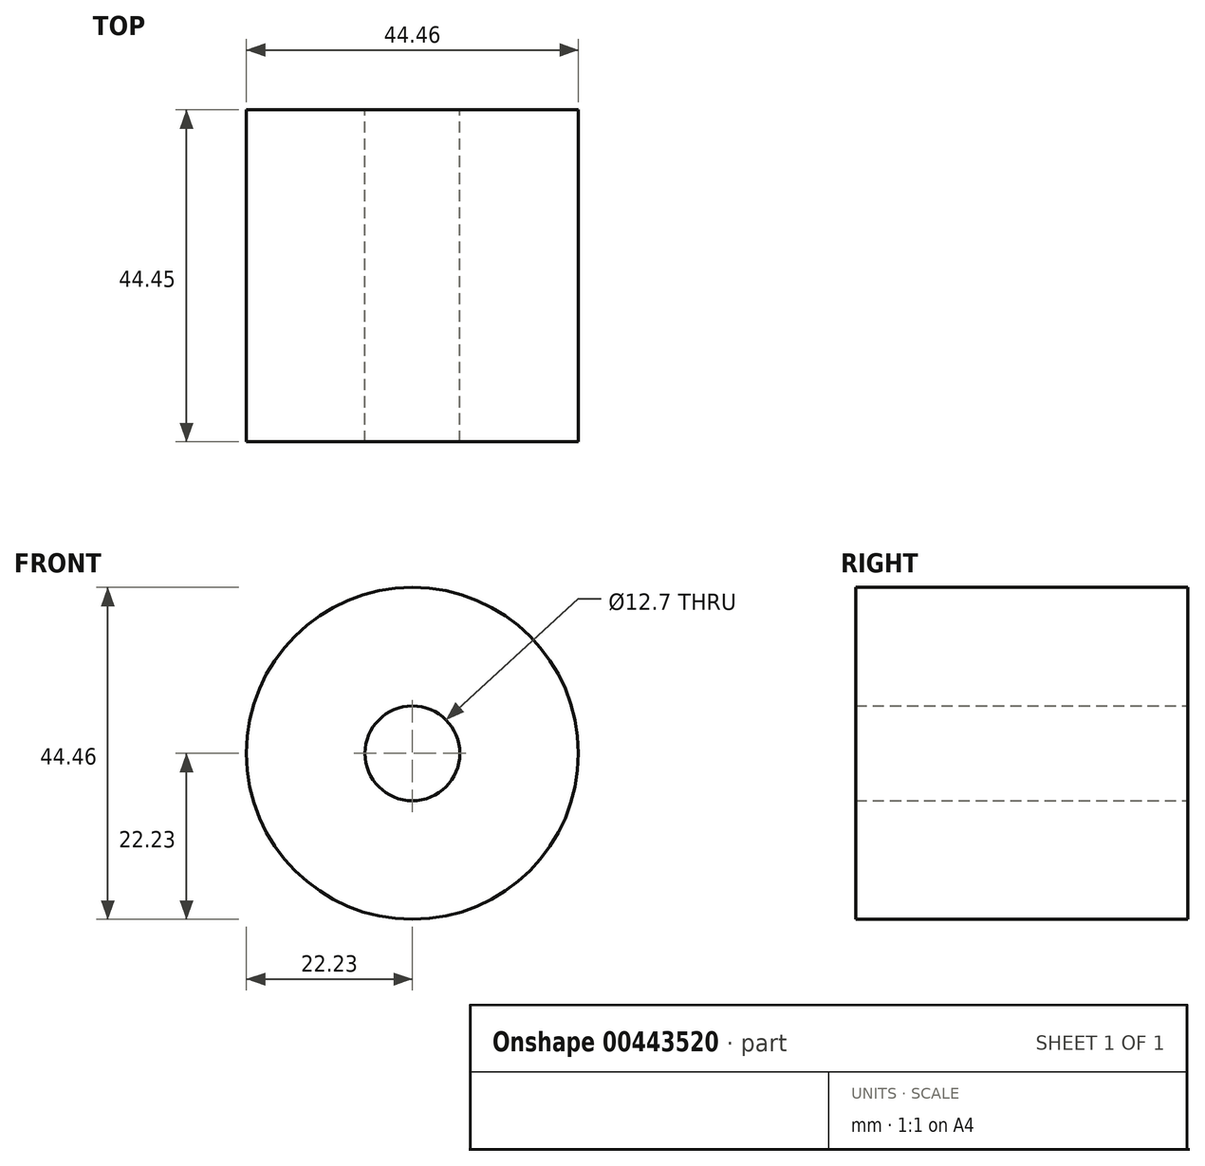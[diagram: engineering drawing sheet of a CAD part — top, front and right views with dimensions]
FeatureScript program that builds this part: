
annotation { "Feature Type Name" : "Feature", "Feature Type Description" : "" }
export const myFeature = defineFeature(function(context is Context, id is Id, definition is map)
    precondition{}
    {
        {
            var Q0;
            Q0=qCreatedBy(makeId("Front.planeOp"),FACE);
            var sketch = newSketch(context, id + "F0", { "sketchPlane" : qUnion([Q0])});
            skCircle(sketch, "E0", {"center": v(0, 0) * mm, "radius": 22.23 * mm});
            skCircle(sketch, "E1", {"center": v(0, 0) * mm, "radius": 6.35 * mm});
            skSolve(sketch);
        }
        {
            var Q0;
            Q0=makeQuery(id+"F0.imprint","IMPRINT",FACE,{"disambiguationData":[TD([[makeQuery(id+"F0.imprint","IMPRINT",EDGE,{"derivedFrom":sQuery(id+"F0.wireOp",EDGE,"E0")}),1.0]])]});
            extrude(context, id + "F1", {"entities" : qUnion([Q0]), "depth" : 44.45 * mm});
        }
    });
